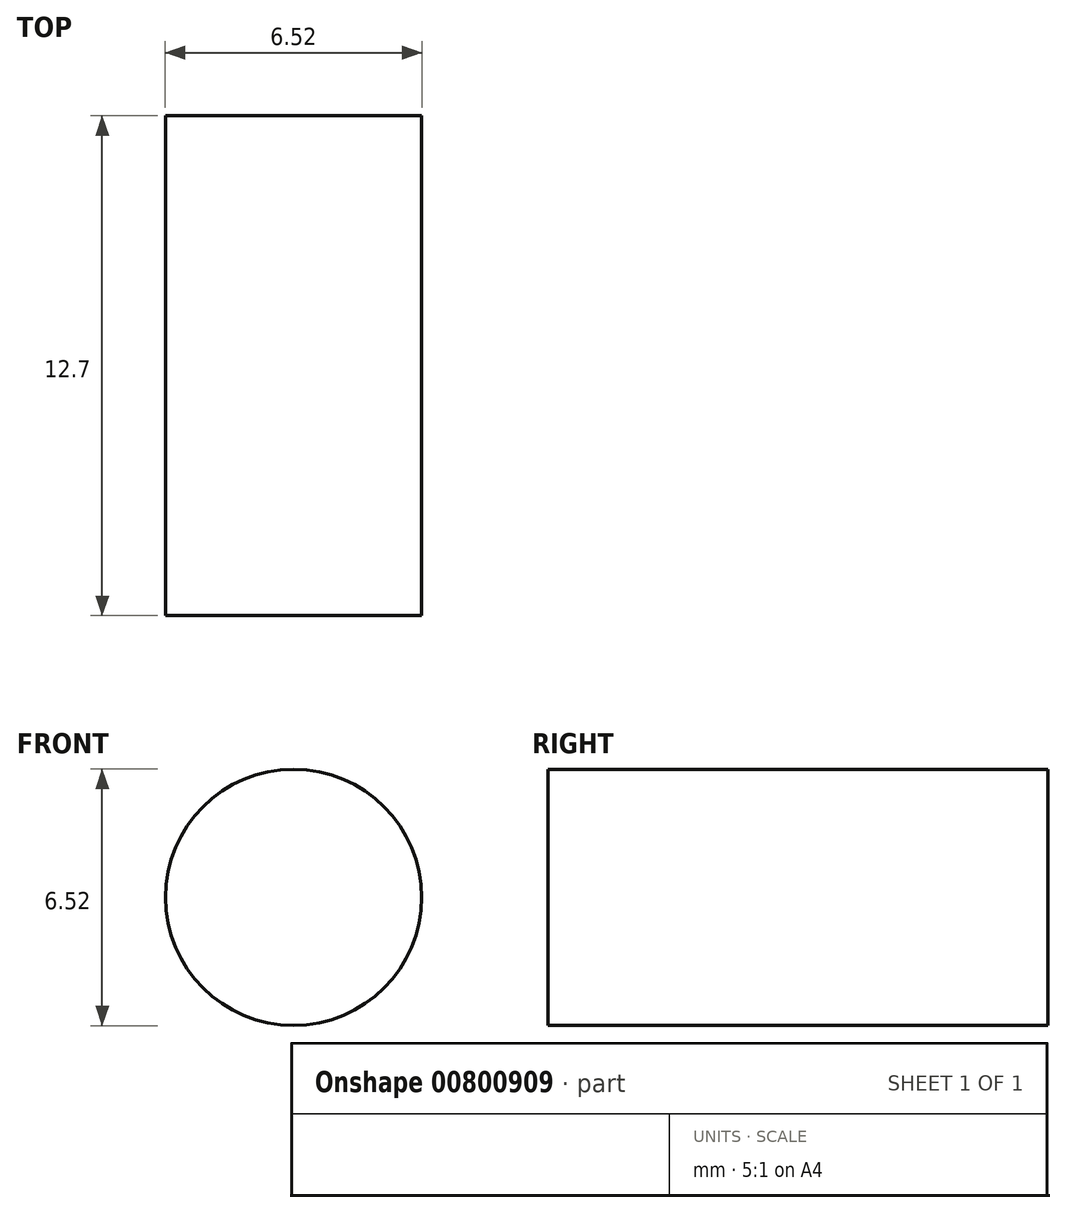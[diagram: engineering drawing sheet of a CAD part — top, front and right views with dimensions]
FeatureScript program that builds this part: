
annotation { "Feature Type Name" : "Feature", "Feature Type Description" : "" }
export const myFeature = defineFeature(function(context is Context, id is Id, definition is map)
    precondition{}
    {
        {
            var Q0;
            Q0=qCreatedBy(makeId("Front.planeOp"),FACE);
            var sketch = newSketch(context, id + "F0", { "sketchPlane" : qUnion([Q0])});
            skCircle(sketch, "E0", {"center": v(0, 0) * mm, "radius": 3.26 * mm});
            skSolve(sketch);
        }
        {
            var Q0;
            Q0 = qSketchRegion(id + "F0", true);
            extrude(context, id + "F1", {"entities" : qUnion([Q0]), "depth" : 12.7 * mm, "offsetDistance" : 25.4 * mm});
        }
    });
